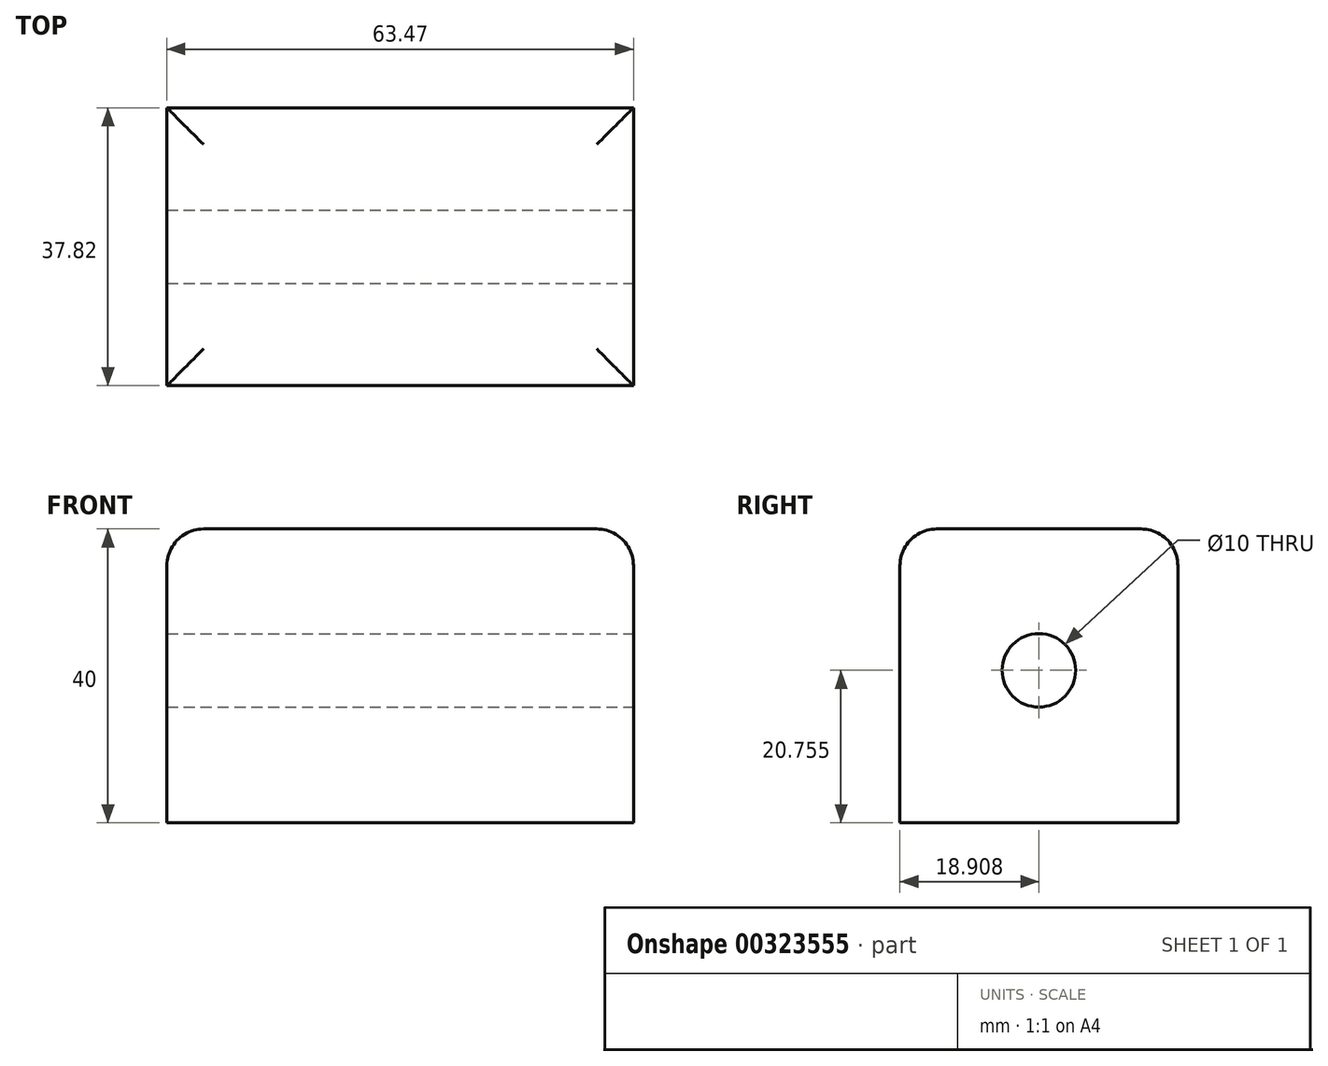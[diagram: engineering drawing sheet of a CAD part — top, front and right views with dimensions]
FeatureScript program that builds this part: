
annotation { "Feature Type Name" : "Feature", "Feature Type Description" : "" }
export const myFeature = defineFeature(function(context is Context, id is Id, definition is map)
    precondition{}
    {
        {
            var Q0;
            Q0=qCreatedBy(makeId("Top.planeOp"),FACE);
            var sketch = newSketch(context, id + "F0", { "sketchPlane" : qUnion([Q0])});
            skLineSegment(sketch, "E0.bottom", {"start": v(0, 0) * mm, "end": v(63.47, 0) * mm});
            skLineSegment(sketch, "E0.top", {"start": v(0, 37.82) * mm, "end": v(63.47, 37.82) * mm});
            skLineSegment(sketch, "E0.left", {"start": v(0, 0) * mm, "end": v(0, 37.82) * mm});
            skLineSegment(sketch, "E0.right", {"start": v(63.47, 0) * mm, "end": v(63.47, 37.82) * mm});
            skLineSegment(sketch, "E1.bottom", {"start": v(31.74, 37.82) * mm, "end": v(14.94, 37.82) * mm});
            skLineSegment(sketch, "E1.top", {"start": v(31.74, 56.65) * mm, "end": v(14.94, 56.65) * mm});
            skLineSegment(sketch, "E1.left", {"start": v(31.74, 37.82) * mm, "end": v(31.74, 56.65) * mm});
            skLineSegment(sketch, "E1.right", {"start": v(14.94, 37.82) * mm, "end": v(14.94, 56.65) * mm});
            skSolve(sketch);
        }
        {
            var Q0;
            Q0=makeQuery(id+"F0.imprint","IMPRINT",FACE,{"disambiguationData":[TD([[makeQuery(id+"F0.imprint","IMPRINT",EDGE,{"derivedFrom":sQuery(id+"F0.wireOp",EDGE,"E1.bottom")}),-1.0]])]});
            var Q1;
            Q1=makeQuery(id+"F0.imprint","IMPRINT",FACE,{"disambiguationData":[TD([[makeQuery(id+"F0.imprint","IMPRINT",EDGE,{"derivedFrom":sQuery(id+"F0.wireOp",EDGE,"E0.bottom")}),1.0]])]});
            extrude(context, id + "F1", {"entities" : qUnion([Q0, Q1]), "depth" : 40 * mm});
        }
        {
            var Q0;
            Q0=makeQuery(id+"F1.opExtrude","CAP_EDGE",EDGE,{"disambiguationData":[OSD([sQuery(id+"F0.wireOp",EDGE,"E1.left")])],"isStart":false});
            var Q1;
            Q1=makeQuery(id+"F1.opExtrude","CAP_EDGE",EDGE,{"disambiguationData":[OSD([sQuery(id+"F0.wireOp",EDGE,"E1.top")])],"isStart":false});
            var Q2;
            Q2=makeQuery(id+"F1.opExtrude","CAP_EDGE",EDGE,{"disambiguationData":[OSD([sQuery(id+"F0.wireOp",EDGE,"E0.bottom")])],"isStart":false});
            var Q3;
            Q3=makeQuery(id+"F1.opExtrude","CAP_EDGE",EDGE,{"disambiguationData":[OSD([sQuery(id+"F0.wireOp",EDGE,"E0.left")])],"isStart":false});
            var Q4;
            {var subQ0=sQuery(id+"F0.wireOp",EDGE,"E0.top");Q4=makeQuery(id+"F1.opExtrude","CAP_EDGE",EDGE,{"disambiguationData":[OSD([subQ0]),TDD([makeQuery(id+"F0.imprint","IMPRINT",EDGE,{"disambiguationData":[TD([[makeQuery(id+"F0.imprint","INTERSECT",VERTEX,{"derivedFrom":[subQ0,sQuery(id+"F0.wireOp",EDGE,"E0.right")]}),1.0]])],"derivedFrom":subQ0})])],"isStart":false});}
            var Q5;
            Q5=makeQuery(id+"F1.opExtrude","CAP_EDGE",EDGE,{"disambiguationData":[OSD([sQuery(id+"F0.wireOp",EDGE,"E0.right")])],"isStart":false});
            var Q6;
            Q6=makeQuery(id+"F1.opExtrude","CAP_EDGE",EDGE,{"disambiguationData":[OSD([sQuery(id+"F0.wireOp",EDGE,"E1.right")])],"isStart":false});
            var Q7;
            {var subQ0=sQuery(id+"F0.wireOp",EDGE,"E0.top");Q7=makeQuery(id+"F1.opExtrude","CAP_EDGE",EDGE,{"disambiguationData":[OSD([subQ0]),TDD([makeQuery(id+"F0.imprint","IMPRINT",EDGE,{"disambiguationData":[TD([[makeQuery(id+"F0.imprint","INTERSECT",VERTEX,{"derivedFrom":[subQ0,sQuery(id+"F0.wireOp",EDGE,"E0.left")]}),-1.0]])],"derivedFrom":subQ0})])],"isStart":false});}
            fillet(context, id + "F2", {"entities" : qUnion([Q0, Q1, Q2, Q3, Q4, Q5, Q6, Q7]), "radius" : 5 * mm, "tangentPropagation" : true, "allowEdgeOverflow" : false});
        }
        {
            var Q0;
            Q0=makeQuery(id+"F1.opExtrude","SWEPT_FACE",FACE,{"disambiguationData":[OSD([sQuery(id+"F0.wireOp",EDGE,"E0.right")])]});
            var sketch = newSketch(context, id + "F3", { "sketchPlane" : qUnion([Q0])});
            skCircle(sketch, "E2", {"center": v(18.9, 20.76) * mm, "radius": 8.58 * mm});
            skPoint(sketch, "E2.centerSnap0", {"position": v(18.9, 35) * mm});
            skSolve(sketch);
        }
        {
            var Q0;
            Q0=sQuery(id+"F3.wireOp",VERTEX,"E2.center");
            var Q1;
            Q1=makeQuery(id+"F1.opExtrude","SWEPT_BODY",BODY,{"disambiguationData":[OSD([sQuery(id+"F0.wireOp",EDGE,"E0.bottom"),sQuery(id+"F0.wireOp",EDGE,"E0.top"),sQuery(id+"F0.wireOp",EDGE,"E0.left"),sQuery(id+"F0.wireOp",EDGE,"E0.right"),sQuery(id+"F0.wireOp",EDGE,"E1.top"),sQuery(id+"F0.wireOp",EDGE,"E1.left"),sQuery(id+"F0.wireOp",EDGE,"E1.right")])]});
            hole(context, id + "F4", {"style" : HoleStyle.SIMPLE, "endStyle" : HoleEndStyle.THROUGH, "standardTappedOrClearance" : lookupTablePath({ "fit" : "Normal", "standard" : "ISO", "size" : "10", "type" : "Gebohrt" }), "standardBlindInLast" : lookupTablePath({ "fit" : "Standard", "standard" : "ISO", "size" : "10", "type" : "Gebohrt" }), "holeDiameter" : 10 * mm, "isTappedThrough" : true, "tappedDepth" : 12 * mm, "tapClearance" : 3, "locations" : qUnion([Q0]), "scope" : qUnion([Q1])});
        }
    });
